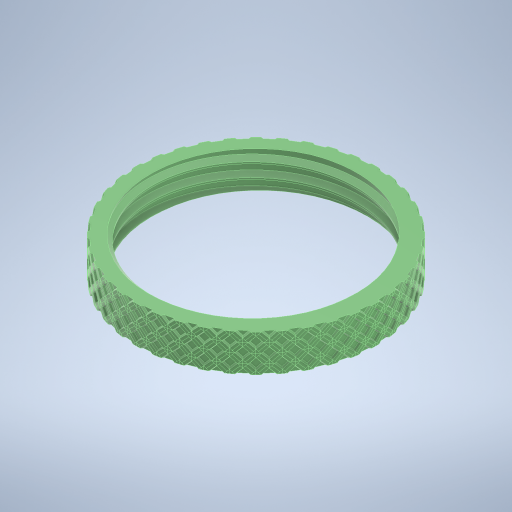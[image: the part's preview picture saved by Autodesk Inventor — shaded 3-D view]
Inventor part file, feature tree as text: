
AUTODESK INVENTOR PART (.ipt)
format: ipt  version: 2024.1 (Build 281209000, 209)  size: 5,713,920 bytes
history: native  units: mm
features: sketch x3, helix x3, extrude x1, draft x1, direct_edit x1, pattern_circular x1, other x1
ambient origin geometry x8: Origin, YZ Plane, XZ Plane, XY Plane, X Axis, Y Axis, Z Axis, Center Point
bodies: Solid1 (feature_tree)
feature tree (11):
  sketch  "Sketch1"  dims[d0=6.806784mm d1=0.55605mm d2=6.806784mm d3=0.6mm d4=12.875mm d5=12.5mm d6=1.047198mm d7=0.896783mm d8=2.25mm]
  extrude  "Extrusion1"  Depth=12.5mm
  draft  "FaceDraft1"
  helix  "Coil1"  [1 undecoded]
  direct_edit  "Direct Edit1"
  sketch  "Sketch3"  dims[d11=29.5mm d12=26.793566mm d13=14.75mm d14=13.899631mm d15=1.290245mm d16=12.875mm d17=0.0mm d18=12.875mm d19=26.794mm d20=2.5mm d21=5.0mm d22=0.0mm d23=1.047198mm d24=2.0mm d25=10.0mm d26=70.0mm d27=-1.047198mm d28=90.0deg d29=90.0deg d30=0.0mm d31=0.0mm d32=-0.25mm d33=0.24mm d34=6.108652mm d35=0.5mm d36=100.0mm d37=5.0mm d38=70.0mm d39=0.0mm d40=90.0deg d41=90.0deg d42=0.0mm d43=0.0mm d44=100.0mm d45=5.0mm d46=70.0mm d47=0.0mm d48=90.0deg d49=90.0deg d50=0.0mm d51=0.0mm d52=400.0mm d53=360.0deg]
  helix  "Coil2"  [1 undecoded]
  helix  "Coil3"  [1 undecoded]
  pattern_circular  "Circular Pattern1"  [2 undecoded]
  sketch  "Sketch2"  dims[d9=90.0deg]
  other  "Size1"
note: 5 required parameter values undecoded (feature->parameter linkage not recoverable at this tier; creation-order binding heuristic only, values carry confidence <= 0.55)
